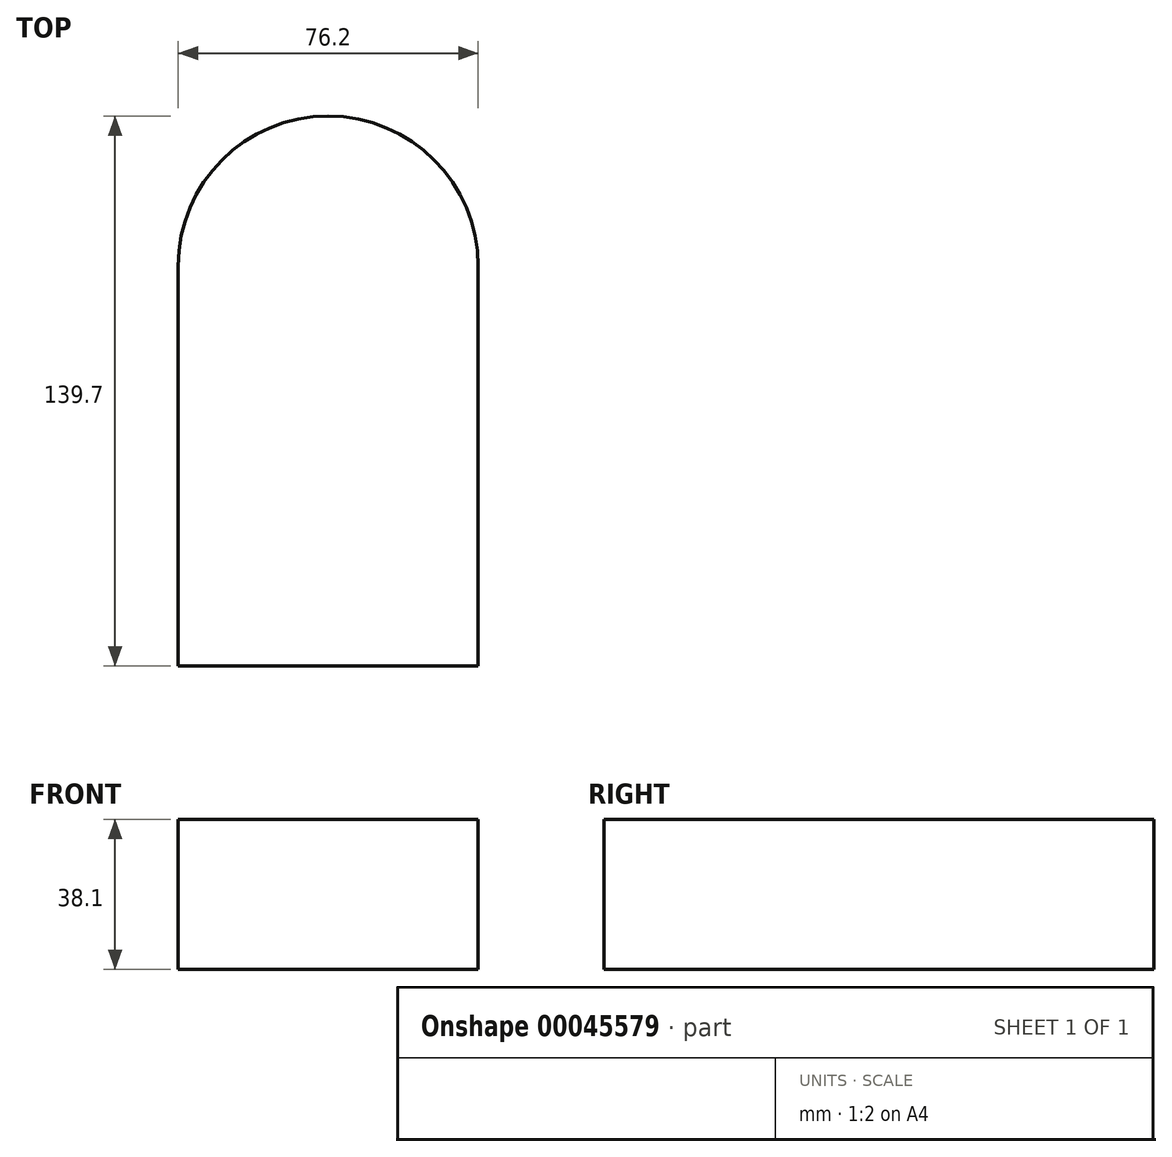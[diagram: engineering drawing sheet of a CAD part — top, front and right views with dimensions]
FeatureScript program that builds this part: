
annotation { "Feature Type Name" : "Feature", "Feature Type Description" : "" }
export const myFeature = defineFeature(function(context is Context, id is Id, definition is map)
    precondition{}
    {
        {
            var Q0;
            Q0=qCreatedBy(makeId("Top.planeOp"),FACE);
            var sketch = newSketch(context, id + "F0", { "sketchPlane" : qUnion([Q0])});
            skLineSegment(sketch, "E0.bottom", {"start": v(-38.1, 50.8) * mm, "end": v(38.1, 50.8) * mm, "construction": true});
            skLineSegment(sketch, "E0.top", {"start": v(-38.1, -50.8) * mm, "end": v(38.1, -50.8) * mm});
            skLineSegment(sketch, "E0.left", {"start": v(-38.1, 50.8) * mm, "end": v(-38.1, -50.8) * mm});
            skLineSegment(sketch, "E0.right", {"start": v(38.1, 50.8) * mm, "end": v(38.1, -50.8) * mm});
            skArc(sketch, "E1", {"start": v(38.1, 50.8) * mm, "mid": v(0, 88.9) * mm, "end": v(-38.1, 50.8) * mm});
            skSolve(sketch);
        }
        {
            var Q0;
            Q0 = qSketchRegion(id + "F0", true);
            extrude(context, id + "F1", {"entities" : qUnion([Q0]), "depth" : 38.1 * mm});
        }
    });
